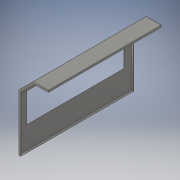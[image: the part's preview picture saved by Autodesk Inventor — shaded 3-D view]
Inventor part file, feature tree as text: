
AUTODESK INVENTOR PART (.ipt)
format: ipt  version: 2018 (Build 220112000, 112)  size: 183,296 bytes
history: native  units: in
note: dims shown in document units (in); Inventor stores cm internally (conversion verified against a paired STEP export)
features: extrude x7, sketch x7, projected_geometry x1
ambient origin geometry x8: Origin, YZ Plane, XZ Plane, XY Plane, X Axis, Y Axis, Z Axis, Center Point
bodies: Solid1 (feature_tree)
feature tree (15):
  extrude  "Extrusion1"  Depth=31.4961in
  extrude  "Extrusion2"  Depth=45.6693in TaperAngle=0.0deg
  extrude  "Extrusion3"  Depth=22.8346in
  extrude  "Extrusion4"  Depth=39.3701in
  extrude  "Extrusion5"  Depth=11.811in
  extrude  "Extrusion6"  Depth=0.063in
  extrude  "Extrusion7"  Depth=0.063in TaperAngle=0.0deg
  sketch  "Sketch1"  dims[d0=6.063in d1=31.4961in]
  sketch  "Sketch2"  dims[d2=135.0deg d6=45.6693in d7=0.0in]
  sketch  "Sketch3"  dims[d8=5.9055in d9=22.8346in]
  sketch  "Sketch4"  dims[d10=2.7559in d13=39.3701in]
  projected_geometry  "Projected Loop1"
  sketch  "Sketch5"  dims[d14=11.811in d16=1.9685in]
  sketch  "Sketch6"  dims[d17=47.2441in d18=0.0in d19=0.063in]
  sketch  "Sketch7"  dims[d20=0.7874in d21=0.063in d22=0.0in d23=0.063in d24=0.0in d25=0.063in d26=0.0in d27=0.063in d28=0.0in d32=0.063in d33=0.7874in d34=0.063in d35=0.7874in d36=0.063in d37=0.0in]
